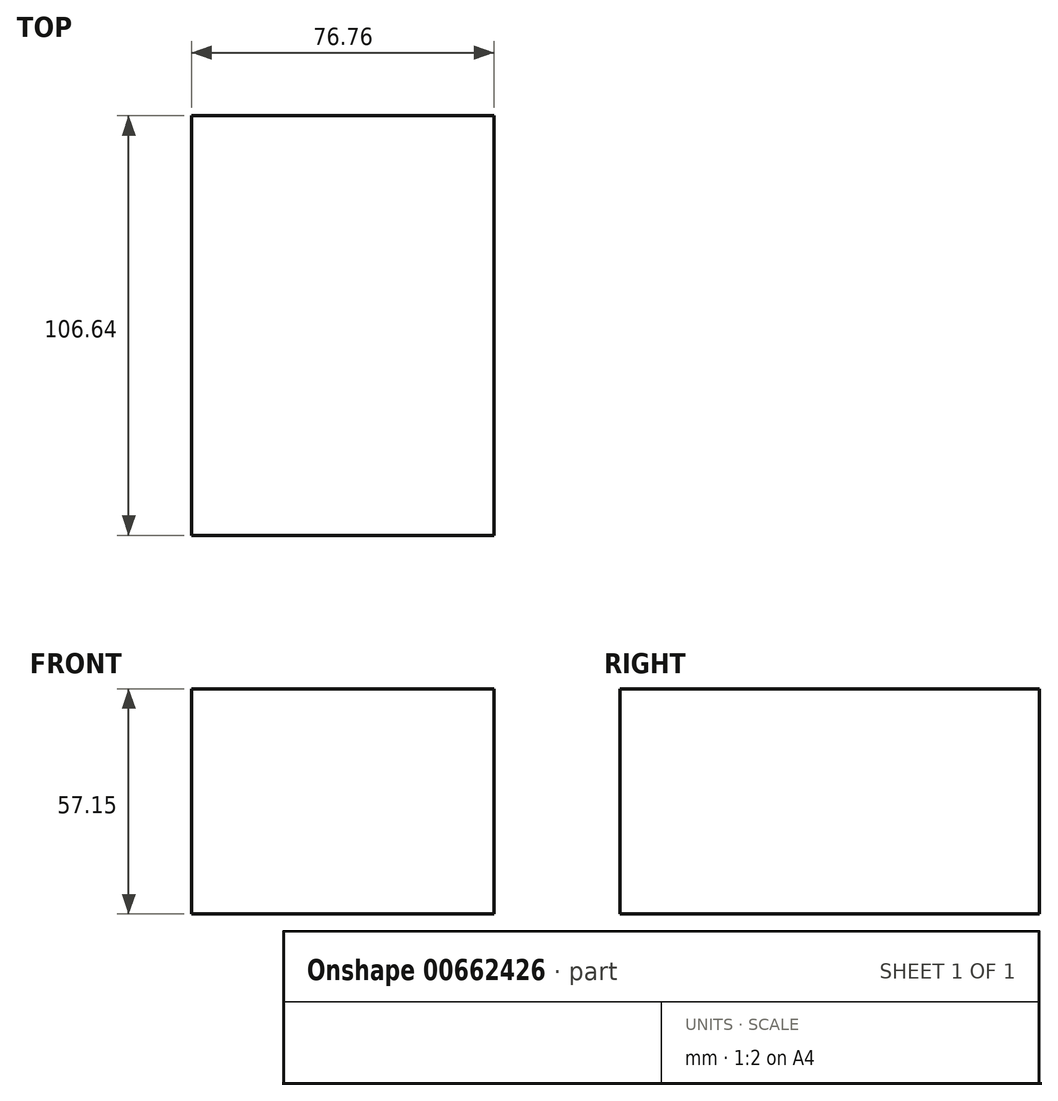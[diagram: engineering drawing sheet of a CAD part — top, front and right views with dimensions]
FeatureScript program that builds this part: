
annotation { "Feature Type Name" : "Feature", "Feature Type Description" : "" }
export const myFeature = defineFeature(function(context is Context, id is Id, definition is map)
    precondition{}
    {
        {
            var Q0;
            Q0=qCreatedBy(makeId("Top.planeOp"),FACE);
            var sketch = newSketch(context, id + "F0", { "sketchPlane" : qUnion([Q0])});
            skLineSegment(sketch, "E0.bottom", {"start": v(38.38, 53.32) * mm, "end": v(-38.38, 53.32) * mm});
            skLineSegment(sketch, "E0.top", {"start": v(38.38, -53.32) * mm, "end": v(-38.38, -53.32) * mm});
            skLineSegment(sketch, "E0.left", {"start": v(38.38, 53.32) * mm, "end": v(38.38, -53.32) * mm});
            skLineSegment(sketch, "E0.right", {"start": v(-38.38, 53.32) * mm, "end": v(-38.38, -53.32) * mm});
            skPoint(sketch, "E0.middle", {"position": v(0, 0) * mm});
            skSolve(sketch);
        }
        {
            var Q0;
            Q0=makeQuery(id+"F0.imprint","IMPRINT",FACE,{"disambiguationData":[TD([[makeQuery(id+"F0.imprint","IMPRINT",EDGE,{"derivedFrom":sQuery(id+"F0.wireOp",EDGE,"E0.bottom")}),1.0]])]});
            extrude(context, id + "F1", {"entities" : qUnion([Q0]), "depth" : 25.4 * mm, "offsetDistance" : 25.4 * mm, "hasSecondDirection" : true, "secondDirectionOppositeDirection" : true, "secondDirectionDepth" : 25.4 * mm});
        }
        {
            var Q0;
            Q0=makeQuery(id+"F1.opExtrude","CAP_FACE",FACE,{"disambiguationData":[OSD([sQuery(id+"F0.wireOp",EDGE,"E0.bottom"),sQuery(id+"F0.wireOp",EDGE,"E0.top"),sQuery(id+"F0.wireOp",EDGE,"E0.left"),sQuery(id+"F0.wireOp",EDGE,"E0.right")])],"isStart":false});
            extrude(context, id + "F2", {"entities" : qUnion([Q0]), "operationType" : NewBodyOperationType.ADD, "depth" : 6.35 * mm, "offsetDistance" : 25.4 * mm});
        }
    });
